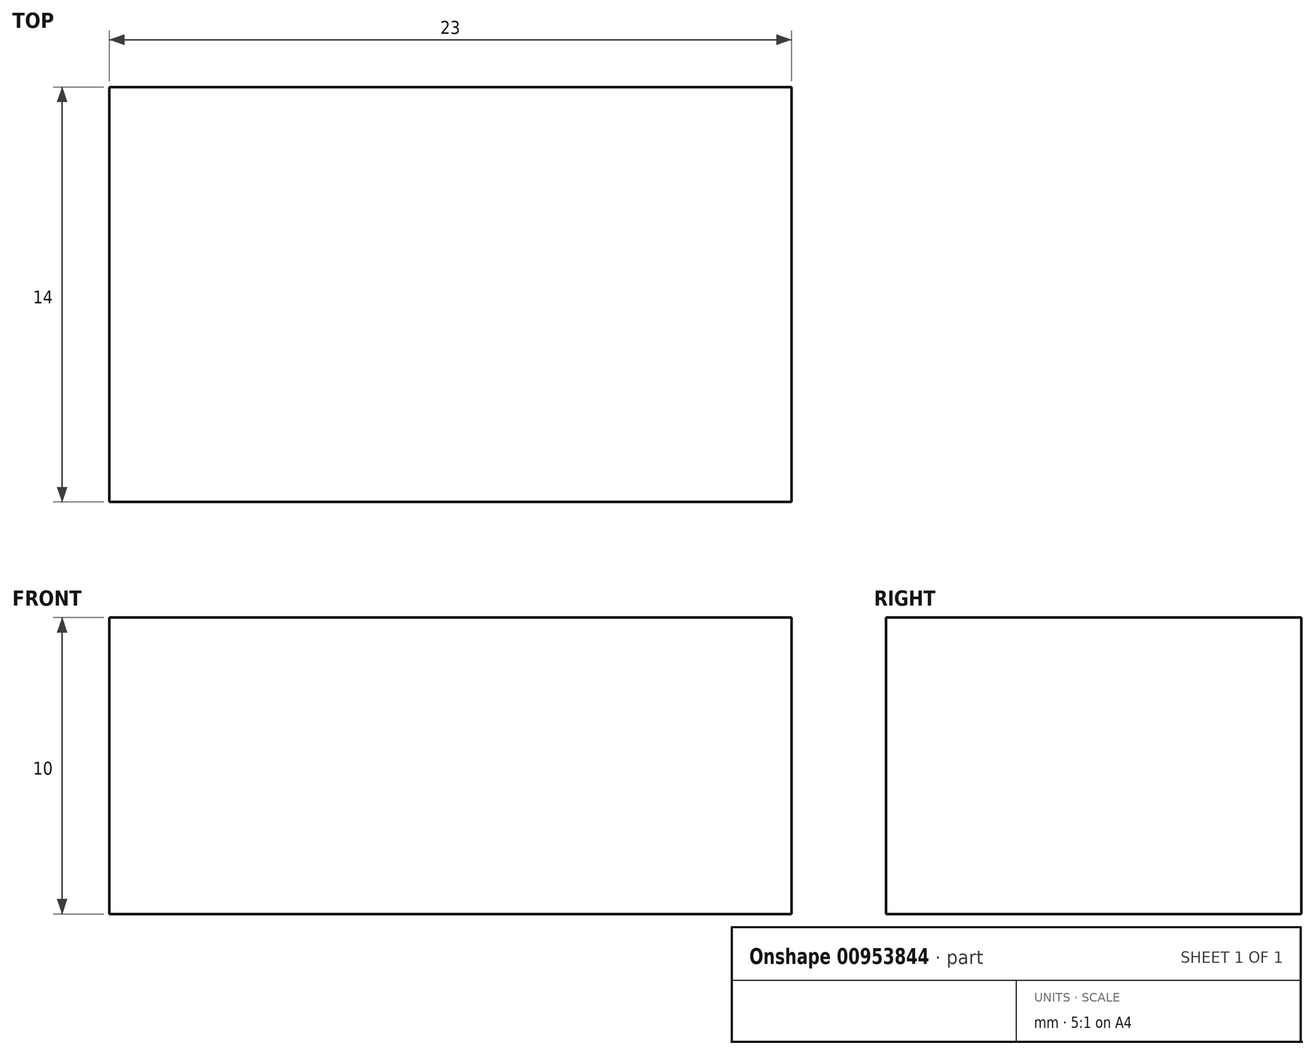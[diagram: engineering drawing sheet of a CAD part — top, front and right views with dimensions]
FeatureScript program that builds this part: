
annotation { "Feature Type Name" : "Feature", "Feature Type Description" : "" }
export const myFeature = defineFeature(function(context is Context, id is Id, definition is map)
    precondition{}
    {
        {
            var Q0;
            Q0=qCreatedBy(makeId("Front.planeOp"),FACE);
            var sketch = newSketch(context, id + "F0", { "sketchPlane" : qUnion([Q0])});
            skLineSegment(sketch, "E0.bottom", {"start": v(11.5, -5) * mm, "end": v(-11.5, -5) * mm});
            skLineSegment(sketch, "E0.top", {"start": v(11.5, 5) * mm, "end": v(-11.5, 5) * mm});
            skLineSegment(sketch, "E0.left", {"start": v(11.5, -5) * mm, "end": v(11.5, 5) * mm});
            skLineSegment(sketch, "E0.right", {"start": v(-11.5, -5) * mm, "end": v(-11.5, 5) * mm});
            skPoint(sketch, "E0.middle", {"position": v(0, 0) * mm});
            skSolve(sketch);
        }
        {
            var Q0;
            Q0=makeQuery(id+"F0.imprint","IMPRINT",FACE,{"disambiguationData":[TD([[makeQuery(id+"F0.imprint","IMPRINT",EDGE,{"derivedFrom":sQuery(id+"F0.wireOp",EDGE,"E0.bottom")}),-1.0]])]});
            extrude(context, id + "F1", {"entities" : qUnion([Q0]), "depth" : 14 * mm, "offsetDistance" : 25 * mm});
        }
    });
